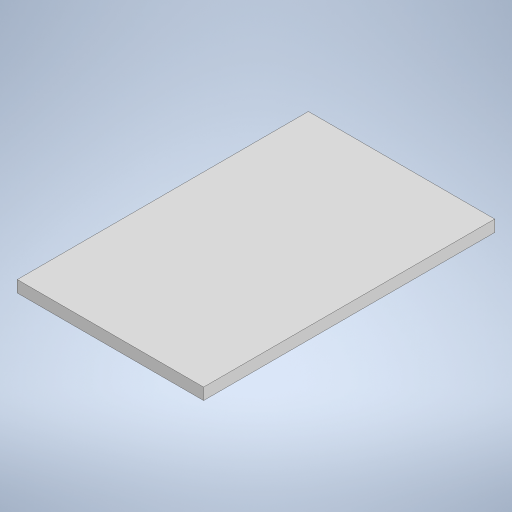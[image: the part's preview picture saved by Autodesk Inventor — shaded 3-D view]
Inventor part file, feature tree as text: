
AUTODESK INVENTOR PART (.ipt)
format: ipt  version: 2024 (Build 280153000, 153)  size: 200,192 bytes
history: native  units: mm
features: extrude x1, sketch x1
ambient origin geometry x8: Origin, YZ Plane, XZ Plane, XY Plane, X Axis, Y Axis, Z Axis, Center Point
bodies: Solid1 (feature_tree)
feature tree (2):
  extrude  "Extrusion1"  Depth=250.0mm
  sketch  "Sketch1"  dims[d0=160.0mm d1=250.0mm d2=10.0mm d3=0.0mm]
